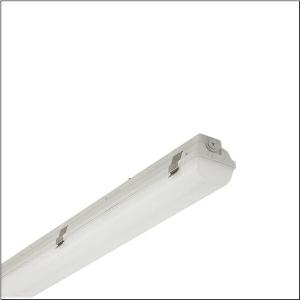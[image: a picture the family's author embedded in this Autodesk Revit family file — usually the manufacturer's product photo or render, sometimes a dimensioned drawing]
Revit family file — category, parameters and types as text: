
# Revit family: monsun_r__21_eco_51fj20dp47a_195a
name_source: partatom
category: Lighting Fixtures
units: mm (PartAtom-declared; Revit-internal decimal feet)

## family parameters
Cut with Voids When Loaded = No
Host = Face
Light Source = No
Part Type = Normal
Room Calculation Point = No
Round Connector Dimension = Use Diameter
Shared = No

## types (1)
- Monsun® 21 Eco (1 x LED, 6600 lm, 50 W, 4000K)
    Apparent Load = 50 VA
    CIE Flux Codes = 40 69 88 88 100
    Color Rendering = 80
    Color Temperature = 4000K
    Default Elevation = 1800 mm
    Description = Monsun® 21 Eco, damp-proof luminaire, primary optical cover: diffuser, of PC, UV-stabilised, frosted, light emission: direct distribution, primary light characteristic: symmetric, installation type: suspended mounting, surface-mounted, LED, rated luminous flux: 6.600lm, luminous efficacy: 132lm/W, light colour: 840, colour temperature: 4000K, control gear: ECG DALI, with terminal, 5-pole, max. 2.5mm², mains connection: 220..240V, AC, 50/60Hz, rated input power: 50W, housing, of glass-fibre reinforced polyester, light grey (RAL 7035), length: 1.577mm, width: 90mm, height: 95mm, clip for enclosure, of spring steel V2A, protection rating (complete): IP66, insulation class (complete): insulation class I (protective earthing), certification: CE, UKCA, protection symbol: D, impact resistance: IK08, permissible operating ambient temperature: -20..+35°C, corresponds to IFS (International Featured Standards) requirements for safety and quality in the food industry, contact your sales advisor before using the luminaires in applications with unclear chemical exposure, large temperature fluctuations or condensation-forming humidity, packaging unit: 1 piece
    Height = 103 mm
    Lamp = 1 x LED
    Lamp Light Flux = 6600 lm
    Lamp Power = 50 W
    Lamp count = 1
    Length = 1577 mm
    Luminous efficacy = 132 lm/W
    Manufacturer = Siteco
    ModVariant = No
    Model = 51FJ20DP47A
    Mounting Place = Ceiling
    Mounting Type = Surface mounted
    Number of Poles = 1
    OnlyDefault = Yes
    Power Factor = 1
    Product Name = Monsun® 21 Eco
    Product group = damp-proof luminaire
    ProductGroupID = 301
    Protection Class = Protection class I
    Protection Degree = IP 66
    RLX_Detail_Level = 1
    RLX_Emergency_Light_Flux = 0 lm
    RLX_Emergency_Type = 0
    RLX_Emergency_Type_DB = No
    RlxData = <blob elided: 33481 chars, md5=ac90af79>
    Socket = socket
    Standby Power = 0 W
    System Light Flux = 6600 lm
    System Power = 50 W
    Type Comments = Product without accessories
    Type Image = l_1007218.jpg
    URL = http://relux.com
    VarID = ---
    Voltage = 0 V
    Weight = 0.00 kg
    Width = 90 mm

## geometry (parser evidence)
native form markers: Blend x4, Sweep x12
no freeform markers — native parametric forms only
